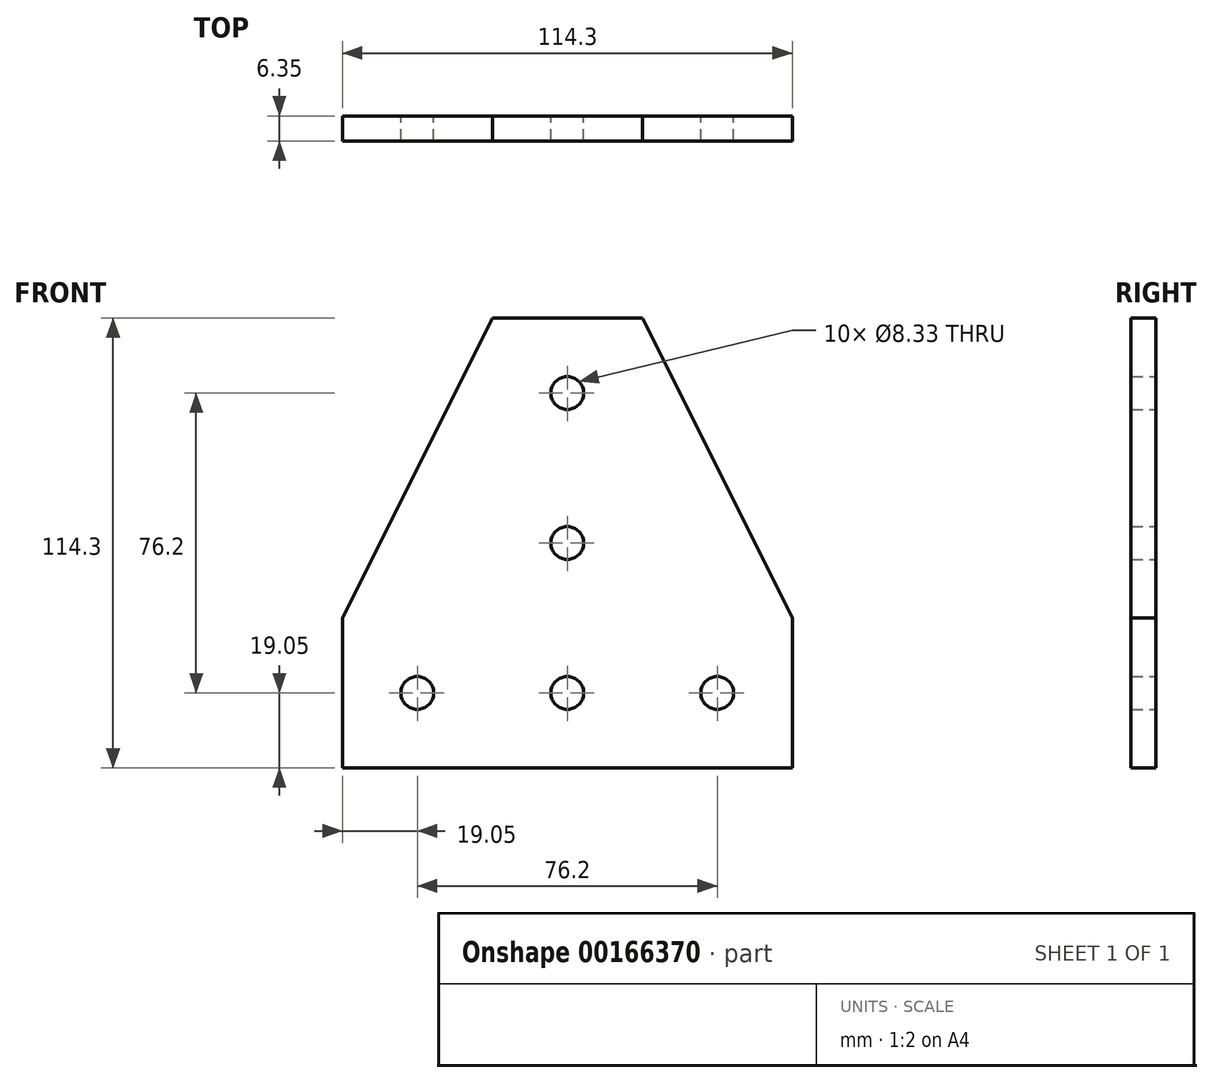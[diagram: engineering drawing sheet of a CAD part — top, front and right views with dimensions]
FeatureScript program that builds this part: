
annotation { "Feature Type Name" : "Feature", "Feature Type Description" : "" }
export const myFeature = defineFeature(function(context is Context, id is Id, definition is map)
    precondition{}
    {
        {
            var Q0;
            Q0=qCreatedBy(makeId("Front.planeOp"),FACE);
            var sketch = newSketch(context, id + "F0", { "sketchPlane" : qUnion([Q0])});
            skLineSegment(sketch, "E0.bottom", {"start": v(57.15, -57.15) * mm, "end": v(-57.15, -57.15) * mm});
            skLineSegment(sketch, "E0.top", {"start": v(19.05, 57.15) * mm, "end": v(-19.05, 57.15) * mm});
            skLineSegment(sketch, "E0.left", {"start": v(57.15, -57.15) * mm, "end": v(57.15, -19.05) * mm});
            skLineSegment(sketch, "E0.right", {"start": v(-57.15, -57.15) * mm, "end": v(-57.15, -19.05) * mm});
            skPoint(sketch, "E0.middle", {"position": v(0, 0) * mm});
            skLineSegment(sketch, "E1", {"start": v(0, -38.1) * mm, "end": v(0, -33.93) * mm});
            skCircle(sketch, "E2", {"center": v(0, 0) * mm, "radius": 4.17 * mm});
            skCircle(sketch, "E3", {"center": v(0, 38.1) * mm, "radius": 4.17 * mm});
            skCircle(sketch, "E4", {"center": v(0, -38.1) * mm, "radius": 4.17 * mm});
            skCircle(sketch, "E5", {"center": v(38.1, -38.1) * mm, "radius": 4.17 * mm});
            skCircle(sketch, "E6", {"center": v(-38.1, -38.1) * mm, "radius": 4.17 * mm});
            skLineSegment(sketch, "E7", {"start": v(0, 57.15) * mm, "end": v(19.05, 57.15) * mm});
            skLineSegment(sketch, "E8", {"start": v(0, 57.15) * mm, "end": v(-19.05, 57.15) * mm});
            skLineSegment(sketch, "E9", {"start": v(-19.05, 57.15) * mm, "end": v(-57.15, -19.05) * mm});
            skLineSegment(sketch, "E10.MirrorCS", {"start": v(19.05, 57.15) * mm, "end": v(57.15, -19.05) * mm});
            skPoint(sketch, "E11.orphan", {"position": v(-57.15, 57.15) * mm});
            skPoint(sketch, "E12.orphan", {"position": v(57.15, 57.15) * mm});
            skPoint(sketch, "E13.orphan", {"position": v(0, -57.15) * mm});
            skSolve(sketch);
        }
        {
            var Q0;
            Q0 = qSketchRegion(id + "F0", true);
            extrude(context, id + "F1", {"entities" : qUnion([Q0]), "depth" : 6.35 * mm});
        }
    });
